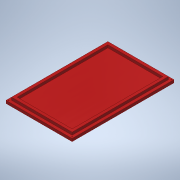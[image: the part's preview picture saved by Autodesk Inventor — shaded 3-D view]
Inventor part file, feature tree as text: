
AUTODESK INVENTOR PART (.ipt)
format: ipt  version: 2022.3 (Build 263350030, 350C)  size: 147,456 bytes
history: native  units: in
note: dims shown in document units (in); Inventor stores cm internally (conversion verified against a paired STEP export)
features: extrude x5, sketch x5
ambient origin geometry x8: Origin, YZ Plane, XZ Plane, XY Plane, X Axis, Y Axis, Z Axis, Center Point
bodies: Solid1 (feature_tree)
feature tree (10):
  extrude  "Extrusion1"  Depth=7.2835in
  extrude  "Extrusion2"  Depth=4.3307in
  extrude  "Extrusion3"  Depth=3.937in
  extrude  "Extrusion4"  Depth=0.1969in TaperAngle=0.0deg
  extrude  "Extrusion5"  Depth=0.0787in
  sketch  "Sketch1"  dims[d0=4.7244in d1=7.2835in]
  sketch  "Sketch2"  dims[d2=0.1969in d3=0.0in d4=4.3307in]
  sketch  "Sketch4"  dims[d5=6.8898in d6=3.937in]
  sketch  "Sketch5"  dims[d7=6.4961in d8=0.1969in d9=0.0in]
  sketch  "Sketch6"  dims[d11=0.128in d12=0.128in d13=0.128in d14=0.1969in d15=0.0in d16=0.128in d17=0.0787in d18=0.0in d19=0.0591in d20=0.0591in d21=0.0591in d22=0.0591in d23=0.0787in d24=0.0in]
